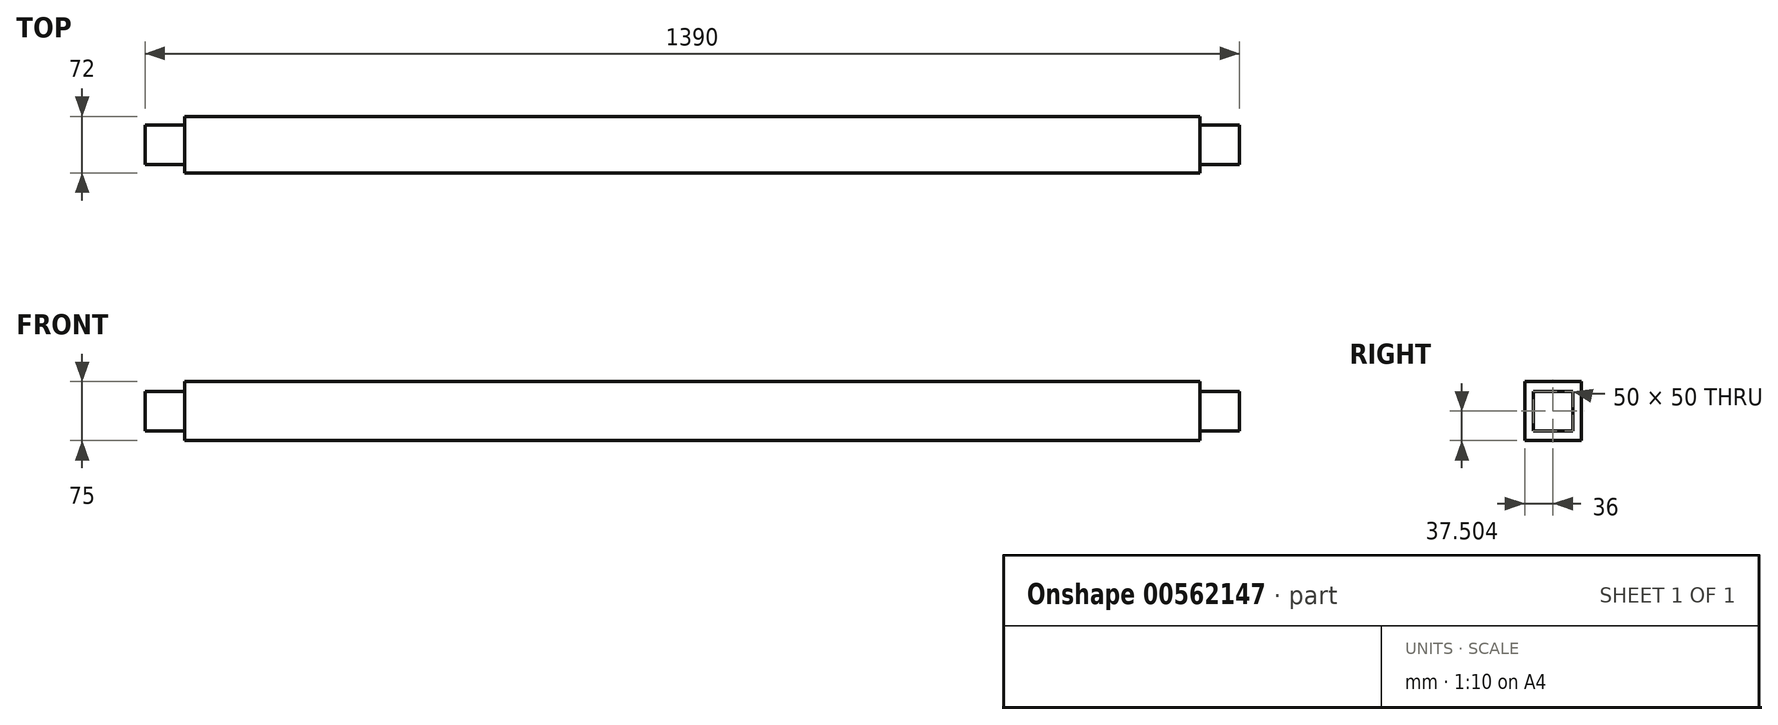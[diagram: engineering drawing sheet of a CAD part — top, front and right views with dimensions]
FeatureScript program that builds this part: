
annotation { "Feature Type Name" : "Feature", "Feature Type Description" : "" }
export const myFeature = defineFeature(function(context is Context, id is Id, definition is map)
    precondition{}
    {
        {
            var Q0;
            Q0=qCreatedBy(makeId("Front.planeOp"),FACE);
            var sketch = newSketch(context, id + "F0", { "sketchPlane" : qUnion([Q0])});
            skLineSegment(sketch, "E0.bottom", {"start": v(-146.89, -32.45) * mm, "end": v(1143.11, -32.45) * mm});
            skLineSegment(sketch, "E0.top", {"start": v(-146.89, 42.55) * mm, "end": v(1143.11, 42.55) * mm});
            skLineSegment(sketch, "E0.left", {"start": v(-146.89, -32.45) * mm, "end": v(-146.89, 42.55) * mm});
            skLineSegment(sketch, "E0.right", {"start": v(1143.11, -32.45) * mm, "end": v(1143.11, 42.55) * mm});
            skSolve(sketch);
        }
        {
            var Q0;
            Q0 = qSketchRegion(id + "F0", true);
            extrude(context, id + "F1", {"entities" : qUnion([Q0]), "depth" : 72 * mm, "offsetDistance" : 25 * mm});
        }
        {
            var Q0;
            Q0=makeQuery(id+"F1.opExtrude","SWEPT_FACE",FACE,{"disambiguationData":[OSD([sQuery(id+"F0.wireOp",EDGE,"E0.right")])]});
            var sketch = newSketch(context, id + "F2", { "sketchPlane" : qUnion([Q0])});
            skLineSegment(sketch, "E1.bottom", {"start": v(-11, -19.95) * mm, "end": v(-61, -19.95) * mm});
            skLineSegment(sketch, "E1.top", {"start": v(-11, 30.05) * mm, "end": v(-61, 30.05) * mm});
            skLineSegment(sketch, "E1.left", {"start": v(-11, -19.95) * mm, "end": v(-11, 30.05) * mm});
            skLineSegment(sketch, "E1.right", {"start": v(-61, -19.95) * mm, "end": v(-61, 30.05) * mm});
            skPoint(sketch, "E1.middle", {"position": v(-36, 5.05) * mm});
            skPoint(sketch, "E1.middle.positionSnap0", {"position": v(-36, 42.55) * mm});
            skPoint(sketch, "E1.middle.positionSnap1", {"position": v(-72, 5.05) * mm});
            skPoint(sketch, "E1.centerSnap0", {"position": v(-36, 42.55) * mm});
            skPoint(sketch, "E1.centerSnap1", {"position": v(-72, 5.05) * mm});
            skLineSegment(sketch, "E2", {"start": v(-11, 30.05) * mm, "end": v(0, 30.05) * mm});
            skLineSegment(sketch, "E3", {"start": v(-61, 30.05) * mm, "end": v(-72, 30.05) * mm});
            skSolve(sketch);
        }
        {
            var Q0;
            Q0 = qSketchRegion(id + "F2", true);
            extrude(context, id + "F3", {"entities" : qUnion([Q0]), "operationType" : NewBodyOperationType.ADD, "depth" : 50 * mm, "offsetDistance" : 25 * mm});
        }
        {
            var Q0;
            Q0=makeQuery(id+"F1.opExtrude","SWEPT_FACE",FACE,{"disambiguationData":[OSD([sQuery(id+"F0.wireOp",EDGE,"E0.left")])]});
            var sketch = newSketch(context, id + "F4", { "sketchPlane" : qUnion([Q0])});
            skLineSegment(sketch, "E4.bottom", {"start": v(11, 30.05) * mm, "end": v(61, 30.05) * mm});
            skLineSegment(sketch, "E4.top", {"start": v(11, -19.95) * mm, "end": v(61, -19.95) * mm});
            skLineSegment(sketch, "E4.left", {"start": v(11, 30.05) * mm, "end": v(11, -19.95) * mm});
            skLineSegment(sketch, "E4.right", {"start": v(61, 30.05) * mm, "end": v(61, -19.95) * mm});
            skPoint(sketch, "E4.middle", {"position": v(36, 5.05) * mm});
            skPoint(sketch, "E4.middle.positionSnap0", {"position": v(72, 5.05) * mm});
            skPoint(sketch, "E4.middle.positionSnap1", {"position": v(36, -32.45) * mm});
            skPoint(sketch, "E4.centerSnap0", {"position": v(72, 5.05) * mm});
            skPoint(sketch, "E4.centerSnap1", {"position": v(36, -32.45) * mm});
            skSolve(sketch);
        }
        {
            var Q0;
            Q0 = qSketchRegion(id + "F4", true);
            extrude(context, id + "F5", {"entities" : qUnion([Q0]), "operationType" : NewBodyOperationType.ADD, "depth" : 50 * mm, "offsetDistance" : 25 * mm});
        }
    });
